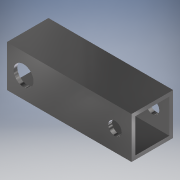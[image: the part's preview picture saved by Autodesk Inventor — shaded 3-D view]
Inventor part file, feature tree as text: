
AUTODESK INVENTOR PART (.ipt)
format: ipt  version: 2018 (Build 220112000, 112)  size: 131,072 bytes
history: native  units: mm
features: extrude x4, sketch x4, other x1
ambient origin geometry x8: Origin, YZ Plane, XZ Plane, XY Plane, X Axis, Y Axis, Z Axis, Center Point
bodies: Body1 (feature_tree)
feature tree (9):
  other  "ソリッド1"
  extrude  "押し出し1"  Depth=25.0mm
  extrude  "押し出し2"  Depth=25.0mm
  extrude  "押し出し3"  Depth=75.0mm TaperAngle=0.0deg
  extrude  "押し出し4"  Depth=12.0mm
  sketch  "スケッチ1"
  sketch  "スケッチ2"
  sketch  "スケッチ3"
  sketch  "スケッチ4"
